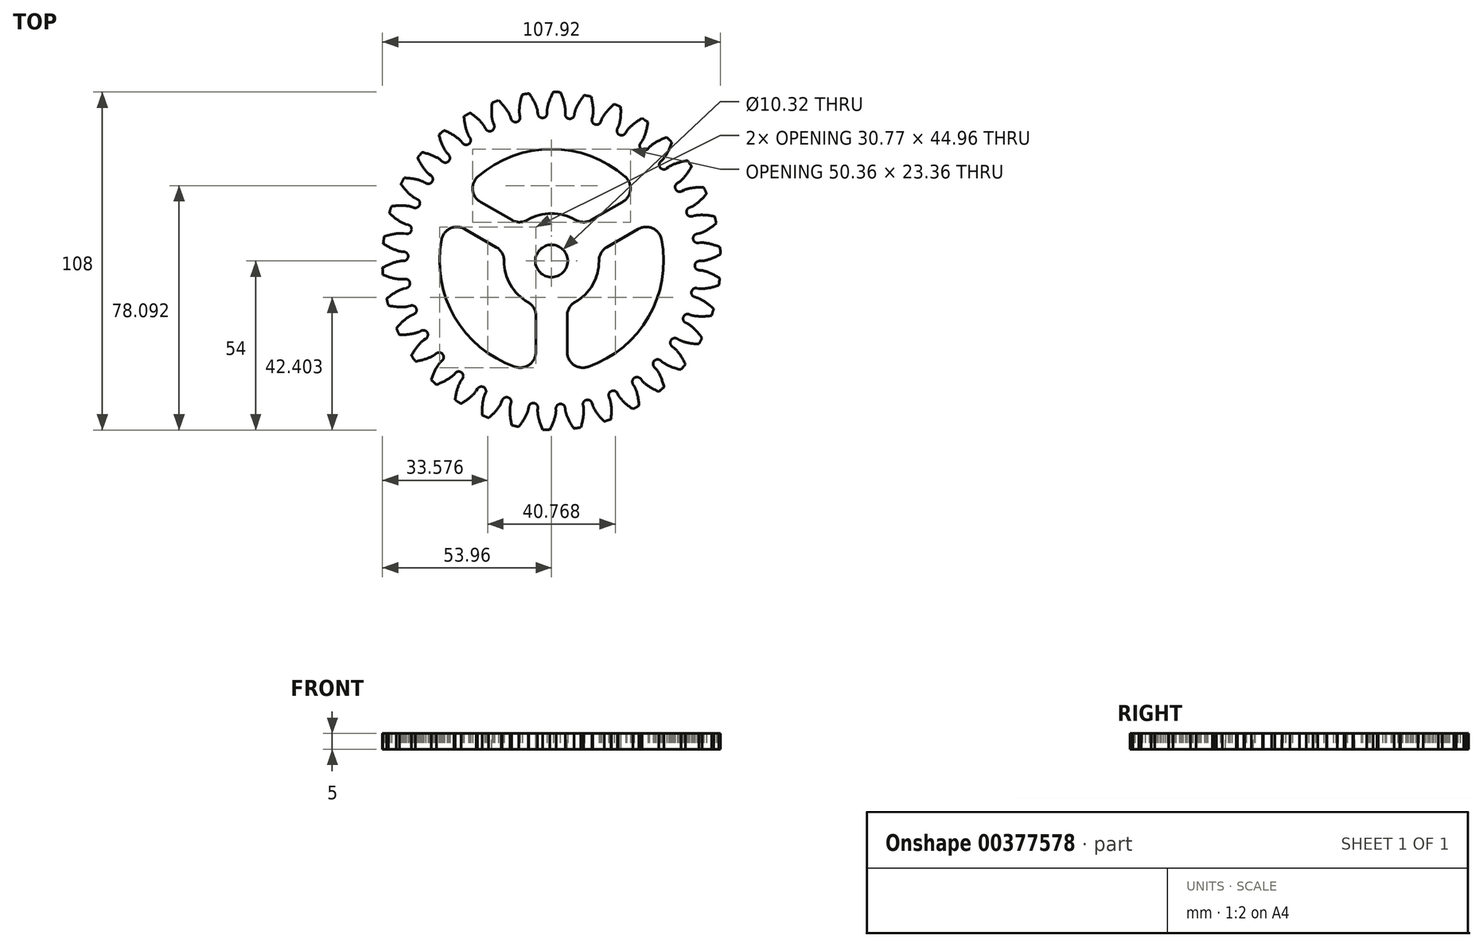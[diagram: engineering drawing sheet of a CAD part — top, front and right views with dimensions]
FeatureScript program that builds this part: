
annotation { "Feature Type Name" : "Feature", "Feature Type Description" : "" }
export const myFeature = defineFeature(function(context is Context, id is Id, definition is map)
    precondition{}
    {
        {
            assignVariable(context, id + "F0", {"name" : "T", "anyValue" : 34});
        }
        {
            assignVariable(context, id + "F1", {"name" : "SP", "anyValue" : 3});
        }
        {
            var Q0;
            Q0=qCreatedBy(makeId("Top.planeOp"),FACE);
            var sketch = newSketch(context, id + "F2", { "sketchPlane" : qUnion([Q0])});
            skCircle(sketch, "E0", {"center": v(0, 0) * mm, "radius": 54 * mm});
            skCircle(sketch, "E1", {"center": v(0, 0) * mm, "radius": 51 * mm, "construction": true});
            skCircle(sketch, "E2", {"center": v(0, 0) * mm, "radius": 47.92 * mm, "construction": true});
            skCircle(sketch, "E3", {"center": v(0, 0) * mm, "radius": 47.25 * mm});
            skLineSegment(sketch, "E4", {"start": v(0, 0) * mm, "end": v(47.92, 0) * mm});
            skFitSpline(sketch, "E5", {"points": [v(47.92, 0) * mm, v(48.06, 0) * mm, v(48.46, 0.05) * mm, v(49.12, 0.18) * mm, v(50.02, 0.42) * mm, v(51.16, 0.82) * mm, v(52.51, 1.42) * mm, v(54.05, 2.23) * mm, v(55.76, 3.3) * mm, v(57.59, 4.66) * mm, v(59.52, 6.32) * mm], "startDerivative": vector(12.01, 0.6) * mm, "endDerivative": vector(39.7, 34.22) * mm});
            skLineSegment(sketch, "E6", {"start": v(0, 0) * mm, "end": v(53.97, -1.69) * mm, "construction": true});
            skLineSegment(sketch, "E7", {"start": v(0, 0) * mm, "end": v(51, 0.76) * mm, "construction": true});
            skFitSpline(sketch, "E8.MirrorCS", {"points": [v(47.83, -3) * mm, v(47.96, -3.01) * mm, v(48.36, -3.08) * mm, v(49, -3.25) * mm, v(49.9, -3.55) * mm, v(51, -4.02) * mm, v(52.32, -4.7) * mm, v(53.8, -5.6) * mm, v(55.44, -6.79) * mm, v(57.18, -8.25) * mm, v(59, -10.03) * mm], "startDerivative": vector(11.95, -1.35) * mm, "endDerivative": vector(37.48, -36.64) * mm});
            skLineSegment(sketch, "E9", {"start": v(0, 0) * mm, "end": v(47.83, -3) * mm});
            skSolve(sketch);
        }
        {
            var Q0;
            Q0=qCreatedBy(makeId("Top.planeOp"),FACE);
            var sketch = newSketch(context, id + "F3", { "sketchPlane" : qUnion([Q0])});
            skCircle(sketch, "E10", {"center": v(0, 0) * mm, "radius": 54 * mm});
            skSolve(sketch);
        }
        {
            var Q0;
            {var subQ0=sQuery(id+"F2.wireOp",EDGE,"E5");var subQ7=sQuery(id+"F2.wireOp",EDGE,"E0");var subQ8=makeQuery(id+"F2.imprint","INTERSECT",VERTEX,{"derivedFrom":[subQ7,subQ0]});Q0=makeQuery(id+"F2.imprint","IMPRINT",FACE,{"disambiguationData":[TD([[makeQuery(id+"F2.imprint","IMPRINT",EDGE,{"disambiguationData":[TD([[subQ8,1.0]])],"derivedFrom":subQ7}),1.0]])]});}
            extrude(context, id + "F4", {"entities" : qUnion([Q0]), "depth" : 6 * mm});
        }
        {
            var Q0;
            Q0=makeQuery(id+"F4.opExtrude","CAP_FACE",FACE,{"disambiguationData":[OSD([sQuery(id+"F2.wireOp",EDGE,"E0"),sQuery(id+"F2.wireOp",EDGE,"E3"),sQuery(id+"F2.wireOp",EDGE,"E4"),sQuery(id+"F2.wireOp",EDGE,"E5"),sQuery(id+"F2.wireOp",EDGE,"E8.MirrorCS"),sQuery(id+"F2.wireOp",EDGE,"E9")])],"isStart":true});
            var sketch = newSketch(context, id + "F5", { "sketchPlane" : qUnion([Q0])});
            skCircle(sketch, "E11", {"center": v(47.23, 1.48) * mm, "radius": 1.48 * mm});
            skSolve(sketch);
        }
        {
            var Q0;
            {var subQ1=makeQuery(id+"F4.opExtrude","CAP_EDGE",EDGE,{"disambiguationData":[OSD([sQuery(id+"F2.wireOp",EDGE,"E3")])],"isStart":true});Q0=makeQuery(id+"F5.imprint","IMPRINT",FACE,{"disambiguationData":[TD([[makeQuery(id+"F5.imprint","IMPRINT",EDGE,{"derivedFrom":subQ1}),-1.0]])]});}
            extrude(context, id + "F6", {"entities" : qUnion([Q0]), "operationType" : NewBodyOperationType.ADD, "oppositeDirection" : true, "depth" : 6 * mm});
        }
        {
            var Q0;
            Q0=makeQuery(id+"F3.imprint","IMPRINT",FACE,{"disambiguationData":[TD([[makeQuery(id+"F3.imprint","IMPRINT",EDGE,{"derivedFrom":sQuery(id+"F3.wireOp",EDGE,"E10")}),1.0]])]});
            extrude(context, id + "F7", {"entities" : qUnion([Q0]), "depth" : 5 * mm});
        }
        {
            var Q0;
            Q0=makeQuery(id+"F4.opExtrude","SWEPT_BODY",BODY,{"disambiguationData":[OSD([sQuery(id+"F2.wireOp",EDGE,"E0"),sQuery(id+"F2.wireOp",EDGE,"E3"),sQuery(id+"F2.wireOp",EDGE,"E4"),sQuery(id+"F2.wireOp",EDGE,"E5"),sQuery(id+"F2.wireOp",EDGE,"E8.MirrorCS"),sQuery(id+"F2.wireOp",EDGE,"E9")])]});
            var Q1;
            Q1=makeQuery(id+"F7.opExtrude","CAP_EDGE",EDGE,{"disambiguationData":[OSD([sQuery(id+"F3.wireOp",EDGE,"E10")])],"isStart":false});
            circularPattern(context, id + "F8", {"entities" : qUnion([Q0]), "axis" : qUnion([Q1]), "angle" : 360 * degree, "instanceCount" : getVariable(context, 'T'), "equalSpace" : true});
        }
        {
            var Q0;
            Q0=makeQuery(id+"F8.opPattern","COPY",BODY,{"derivedFrom":makeQuery(id+"F4.opExtrude","SWEPT_BODY",BODY,{"disambiguationData":[OSD([sQuery(id+"F2.wireOp",EDGE,"E0"),sQuery(id+"F2.wireOp",EDGE,"E3"),sQuery(id+"F2.wireOp",EDGE,"E4"),sQuery(id+"F2.wireOp",EDGE,"E5"),sQuery(id+"F2.wireOp",EDGE,"E8.MirrorCS"),sQuery(id+"F2.wireOp",EDGE,"E9")])]}),"instanceName":"5"});
            var Q1;
            Q1=makeQuery(id+"F8.opPattern","COPY",BODY,{"derivedFrom":makeQuery(id+"F4.opExtrude","SWEPT_BODY",BODY,{"disambiguationData":[OSD([sQuery(id+"F2.wireOp",EDGE,"E0"),sQuery(id+"F2.wireOp",EDGE,"E3"),sQuery(id+"F2.wireOp",EDGE,"E4"),sQuery(id+"F2.wireOp",EDGE,"E5"),sQuery(id+"F2.wireOp",EDGE,"E8.MirrorCS"),sQuery(id+"F2.wireOp",EDGE,"E9")])]}),"instanceName":"6"});
            var Q2;
            Q2=makeQuery(id+"F8.opPattern","COPY",BODY,{"derivedFrom":makeQuery(id+"F4.opExtrude","SWEPT_BODY",BODY,{"disambiguationData":[OSD([sQuery(id+"F2.wireOp",EDGE,"E0"),sQuery(id+"F2.wireOp",EDGE,"E3"),sQuery(id+"F2.wireOp",EDGE,"E4"),sQuery(id+"F2.wireOp",EDGE,"E5"),sQuery(id+"F2.wireOp",EDGE,"E8.MirrorCS"),sQuery(id+"F2.wireOp",EDGE,"E9")])]}),"instanceName":"7"});
            var Q3;
            Q3=makeQuery(id+"F8.opPattern","COPY",BODY,{"derivedFrom":makeQuery(id+"F4.opExtrude","SWEPT_BODY",BODY,{"disambiguationData":[OSD([sQuery(id+"F2.wireOp",EDGE,"E0"),sQuery(id+"F2.wireOp",EDGE,"E3"),sQuery(id+"F2.wireOp",EDGE,"E4"),sQuery(id+"F2.wireOp",EDGE,"E5"),sQuery(id+"F2.wireOp",EDGE,"E8.MirrorCS"),sQuery(id+"F2.wireOp",EDGE,"E9")])]}),"instanceName":"8"});
            var Q4;
            Q4=makeQuery(id+"F8.opPattern","COPY",BODY,{"derivedFrom":makeQuery(id+"F4.opExtrude","SWEPT_BODY",BODY,{"disambiguationData":[OSD([sQuery(id+"F2.wireOp",EDGE,"E0"),sQuery(id+"F2.wireOp",EDGE,"E3"),sQuery(id+"F2.wireOp",EDGE,"E4"),sQuery(id+"F2.wireOp",EDGE,"E5"),sQuery(id+"F2.wireOp",EDGE,"E8.MirrorCS"),sQuery(id+"F2.wireOp",EDGE,"E9")])]}),"instanceName":"9"});
            var Q5;
            Q5=makeQuery(id+"F8.opPattern","COPY",BODY,{"derivedFrom":makeQuery(id+"F4.opExtrude","SWEPT_BODY",BODY,{"disambiguationData":[OSD([sQuery(id+"F2.wireOp",EDGE,"E0"),sQuery(id+"F2.wireOp",EDGE,"E3"),sQuery(id+"F2.wireOp",EDGE,"E4"),sQuery(id+"F2.wireOp",EDGE,"E5"),sQuery(id+"F2.wireOp",EDGE,"E8.MirrorCS"),sQuery(id+"F2.wireOp",EDGE,"E9")])]}),"instanceName":"10"});
            var Q6;
            Q6=makeQuery(id+"F8.opPattern","COPY",BODY,{"derivedFrom":makeQuery(id+"F4.opExtrude","SWEPT_BODY",BODY,{"disambiguationData":[OSD([sQuery(id+"F2.wireOp",EDGE,"E0"),sQuery(id+"F2.wireOp",EDGE,"E3"),sQuery(id+"F2.wireOp",EDGE,"E4"),sQuery(id+"F2.wireOp",EDGE,"E5"),sQuery(id+"F2.wireOp",EDGE,"E8.MirrorCS"),sQuery(id+"F2.wireOp",EDGE,"E9")])]}),"instanceName":"11"});
            var Q7;
            Q7=makeQuery(id+"F8.opPattern","COPY",BODY,{"derivedFrom":makeQuery(id+"F4.opExtrude","SWEPT_BODY",BODY,{"disambiguationData":[OSD([sQuery(id+"F2.wireOp",EDGE,"E0"),sQuery(id+"F2.wireOp",EDGE,"E3"),sQuery(id+"F2.wireOp",EDGE,"E4"),sQuery(id+"F2.wireOp",EDGE,"E5"),sQuery(id+"F2.wireOp",EDGE,"E8.MirrorCS"),sQuery(id+"F2.wireOp",EDGE,"E9")])]}),"instanceName":"12"});
            var Q8;
            Q8=makeQuery(id+"F8.opPattern","COPY",BODY,{"derivedFrom":makeQuery(id+"F4.opExtrude","SWEPT_BODY",BODY,{"disambiguationData":[OSD([sQuery(id+"F2.wireOp",EDGE,"E0"),sQuery(id+"F2.wireOp",EDGE,"E3"),sQuery(id+"F2.wireOp",EDGE,"E4"),sQuery(id+"F2.wireOp",EDGE,"E5"),sQuery(id+"F2.wireOp",EDGE,"E8.MirrorCS"),sQuery(id+"F2.wireOp",EDGE,"E9")])]}),"instanceName":"13"});
            var Q9;
            Q9=makeQuery(id+"F8.opPattern","COPY",BODY,{"derivedFrom":makeQuery(id+"F4.opExtrude","SWEPT_BODY",BODY,{"disambiguationData":[OSD([sQuery(id+"F2.wireOp",EDGE,"E0"),sQuery(id+"F2.wireOp",EDGE,"E3"),sQuery(id+"F2.wireOp",EDGE,"E4"),sQuery(id+"F2.wireOp",EDGE,"E5"),sQuery(id+"F2.wireOp",EDGE,"E8.MirrorCS"),sQuery(id+"F2.wireOp",EDGE,"E9")])]}),"instanceName":"14"});
            var Q10;
            Q10=makeQuery(id+"F8.opPattern","COPY",BODY,{"derivedFrom":makeQuery(id+"F4.opExtrude","SWEPT_BODY",BODY,{"disambiguationData":[OSD([sQuery(id+"F2.wireOp",EDGE,"E0"),sQuery(id+"F2.wireOp",EDGE,"E3"),sQuery(id+"F2.wireOp",EDGE,"E4"),sQuery(id+"F2.wireOp",EDGE,"E5"),sQuery(id+"F2.wireOp",EDGE,"E8.MirrorCS"),sQuery(id+"F2.wireOp",EDGE,"E9")])]}),"instanceName":"15"});
            var Q11;
            Q11=makeQuery(id+"F8.opPattern","COPY",BODY,{"derivedFrom":makeQuery(id+"F4.opExtrude","SWEPT_BODY",BODY,{"disambiguationData":[OSD([sQuery(id+"F2.wireOp",EDGE,"E0"),sQuery(id+"F2.wireOp",EDGE,"E3"),sQuery(id+"F2.wireOp",EDGE,"E4"),sQuery(id+"F2.wireOp",EDGE,"E5"),sQuery(id+"F2.wireOp",EDGE,"E8.MirrorCS"),sQuery(id+"F2.wireOp",EDGE,"E9")])]}),"instanceName":"16"});
            var Q12;
            Q12=makeQuery(id+"F8.opPattern","COPY",BODY,{"derivedFrom":makeQuery(id+"F4.opExtrude","SWEPT_BODY",BODY,{"disambiguationData":[OSD([sQuery(id+"F2.wireOp",EDGE,"E0"),sQuery(id+"F2.wireOp",EDGE,"E3"),sQuery(id+"F2.wireOp",EDGE,"E4"),sQuery(id+"F2.wireOp",EDGE,"E5"),sQuery(id+"F2.wireOp",EDGE,"E8.MirrorCS"),sQuery(id+"F2.wireOp",EDGE,"E9")])]}),"instanceName":"17"});
            var Q13;
            Q13=makeQuery(id+"F8.opPattern","COPY",BODY,{"derivedFrom":makeQuery(id+"F4.opExtrude","SWEPT_BODY",BODY,{"disambiguationData":[OSD([sQuery(id+"F2.wireOp",EDGE,"E0"),sQuery(id+"F2.wireOp",EDGE,"E3"),sQuery(id+"F2.wireOp",EDGE,"E4"),sQuery(id+"F2.wireOp",EDGE,"E5"),sQuery(id+"F2.wireOp",EDGE,"E8.MirrorCS"),sQuery(id+"F2.wireOp",EDGE,"E9")])]}),"instanceName":"18"});
            var Q14;
            Q14=makeQuery(id+"F8.opPattern","COPY",BODY,{"derivedFrom":makeQuery(id+"F4.opExtrude","SWEPT_BODY",BODY,{"disambiguationData":[OSD([sQuery(id+"F2.wireOp",EDGE,"E0"),sQuery(id+"F2.wireOp",EDGE,"E3"),sQuery(id+"F2.wireOp",EDGE,"E4"),sQuery(id+"F2.wireOp",EDGE,"E5"),sQuery(id+"F2.wireOp",EDGE,"E8.MirrorCS"),sQuery(id+"F2.wireOp",EDGE,"E9")])]}),"instanceName":"19"});
            var Q15;
            Q15=makeQuery(id+"F8.opPattern","COPY",BODY,{"derivedFrom":makeQuery(id+"F4.opExtrude","SWEPT_BODY",BODY,{"disambiguationData":[OSD([sQuery(id+"F2.wireOp",EDGE,"E0"),sQuery(id+"F2.wireOp",EDGE,"E3"),sQuery(id+"F2.wireOp",EDGE,"E4"),sQuery(id+"F2.wireOp",EDGE,"E5"),sQuery(id+"F2.wireOp",EDGE,"E8.MirrorCS"),sQuery(id+"F2.wireOp",EDGE,"E9")])]}),"instanceName":"20"});
            var Q16;
            Q16=makeQuery(id+"F8.opPattern","COPY",BODY,{"derivedFrom":makeQuery(id+"F4.opExtrude","SWEPT_BODY",BODY,{"disambiguationData":[OSD([sQuery(id+"F2.wireOp",EDGE,"E0"),sQuery(id+"F2.wireOp",EDGE,"E3"),sQuery(id+"F2.wireOp",EDGE,"E4"),sQuery(id+"F2.wireOp",EDGE,"E5"),sQuery(id+"F2.wireOp",EDGE,"E8.MirrorCS"),sQuery(id+"F2.wireOp",EDGE,"E9")])]}),"instanceName":"21"});
            var Q17;
            Q17=makeQuery(id+"F8.opPattern","COPY",BODY,{"derivedFrom":makeQuery(id+"F4.opExtrude","SWEPT_BODY",BODY,{"disambiguationData":[OSD([sQuery(id+"F2.wireOp",EDGE,"E0"),sQuery(id+"F2.wireOp",EDGE,"E3"),sQuery(id+"F2.wireOp",EDGE,"E4"),sQuery(id+"F2.wireOp",EDGE,"E5"),sQuery(id+"F2.wireOp",EDGE,"E8.MirrorCS"),sQuery(id+"F2.wireOp",EDGE,"E9")])]}),"instanceName":"22"});
            var Q18;
            Q18=makeQuery(id+"F8.opPattern","COPY",BODY,{"derivedFrom":makeQuery(id+"F4.opExtrude","SWEPT_BODY",BODY,{"disambiguationData":[OSD([sQuery(id+"F2.wireOp",EDGE,"E0"),sQuery(id+"F2.wireOp",EDGE,"E3"),sQuery(id+"F2.wireOp",EDGE,"E4"),sQuery(id+"F2.wireOp",EDGE,"E5"),sQuery(id+"F2.wireOp",EDGE,"E8.MirrorCS"),sQuery(id+"F2.wireOp",EDGE,"E9")])]}),"instanceName":"23"});
            var Q19;
            Q19=makeQuery(id+"F8.opPattern","COPY",BODY,{"derivedFrom":makeQuery(id+"F4.opExtrude","SWEPT_BODY",BODY,{"disambiguationData":[OSD([sQuery(id+"F2.wireOp",EDGE,"E0"),sQuery(id+"F2.wireOp",EDGE,"E3"),sQuery(id+"F2.wireOp",EDGE,"E4"),sQuery(id+"F2.wireOp",EDGE,"E5"),sQuery(id+"F2.wireOp",EDGE,"E8.MirrorCS"),sQuery(id+"F2.wireOp",EDGE,"E9")])]}),"instanceName":"24"});
            var Q20;
            Q20=makeQuery(id+"F8.opPattern","COPY",BODY,{"derivedFrom":makeQuery(id+"F4.opExtrude","SWEPT_BODY",BODY,{"disambiguationData":[OSD([sQuery(id+"F2.wireOp",EDGE,"E0"),sQuery(id+"F2.wireOp",EDGE,"E3"),sQuery(id+"F2.wireOp",EDGE,"E4"),sQuery(id+"F2.wireOp",EDGE,"E5"),sQuery(id+"F2.wireOp",EDGE,"E8.MirrorCS"),sQuery(id+"F2.wireOp",EDGE,"E9")])]}),"instanceName":"25"});
            var Q21;
            Q21=makeQuery(id+"F8.opPattern","COPY",BODY,{"derivedFrom":makeQuery(id+"F4.opExtrude","SWEPT_BODY",BODY,{"disambiguationData":[OSD([sQuery(id+"F2.wireOp",EDGE,"E0"),sQuery(id+"F2.wireOp",EDGE,"E3"),sQuery(id+"F2.wireOp",EDGE,"E4"),sQuery(id+"F2.wireOp",EDGE,"E5"),sQuery(id+"F2.wireOp",EDGE,"E8.MirrorCS"),sQuery(id+"F2.wireOp",EDGE,"E9")])]}),"instanceName":"26"});
            var Q22;
            Q22=makeQuery(id+"F8.opPattern","COPY",BODY,{"derivedFrom":makeQuery(id+"F4.opExtrude","SWEPT_BODY",BODY,{"disambiguationData":[OSD([sQuery(id+"F2.wireOp",EDGE,"E0"),sQuery(id+"F2.wireOp",EDGE,"E3"),sQuery(id+"F2.wireOp",EDGE,"E4"),sQuery(id+"F2.wireOp",EDGE,"E5"),sQuery(id+"F2.wireOp",EDGE,"E8.MirrorCS"),sQuery(id+"F2.wireOp",EDGE,"E9")])]}),"instanceName":"27"});
            var Q23;
            Q23=makeQuery(id+"F8.opPattern","COPY",BODY,{"derivedFrom":makeQuery(id+"F4.opExtrude","SWEPT_BODY",BODY,{"disambiguationData":[OSD([sQuery(id+"F2.wireOp",EDGE,"E0"),sQuery(id+"F2.wireOp",EDGE,"E3"),sQuery(id+"F2.wireOp",EDGE,"E4"),sQuery(id+"F2.wireOp",EDGE,"E5"),sQuery(id+"F2.wireOp",EDGE,"E8.MirrorCS"),sQuery(id+"F2.wireOp",EDGE,"E9")])]}),"instanceName":"28"});
            var Q24;
            Q24=makeQuery(id+"F8.opPattern","COPY",BODY,{"derivedFrom":makeQuery(id+"F4.opExtrude","SWEPT_BODY",BODY,{"disambiguationData":[OSD([sQuery(id+"F2.wireOp",EDGE,"E0"),sQuery(id+"F2.wireOp",EDGE,"E3"),sQuery(id+"F2.wireOp",EDGE,"E4"),sQuery(id+"F2.wireOp",EDGE,"E5"),sQuery(id+"F2.wireOp",EDGE,"E8.MirrorCS"),sQuery(id+"F2.wireOp",EDGE,"E9")])]}),"instanceName":"29"});
            var Q25;
            Q25=makeQuery(id+"F4.opExtrude","SWEPT_BODY",BODY,{"disambiguationData":[OSD([sQuery(id+"F2.wireOp",EDGE,"E0"),sQuery(id+"F2.wireOp",EDGE,"E3"),sQuery(id+"F2.wireOp",EDGE,"E4"),sQuery(id+"F2.wireOp",EDGE,"E5"),sQuery(id+"F2.wireOp",EDGE,"E8.MirrorCS"),sQuery(id+"F2.wireOp",EDGE,"E9")])]});
            var Q26;
            Q26=makeQuery(id+"F8.opPattern","COPY",BODY,{"derivedFrom":makeQuery(id+"F4.opExtrude","SWEPT_BODY",BODY,{"disambiguationData":[OSD([sQuery(id+"F2.wireOp",EDGE,"E0"),sQuery(id+"F2.wireOp",EDGE,"E3"),sQuery(id+"F2.wireOp",EDGE,"E4"),sQuery(id+"F2.wireOp",EDGE,"E5"),sQuery(id+"F2.wireOp",EDGE,"E8.MirrorCS"),sQuery(id+"F2.wireOp",EDGE,"E9")])]}),"instanceName":"1"});
            var Q27;
            Q27=makeQuery(id+"F8.opPattern","COPY",BODY,{"derivedFrom":makeQuery(id+"F4.opExtrude","SWEPT_BODY",BODY,{"disambiguationData":[OSD([sQuery(id+"F2.wireOp",EDGE,"E0"),sQuery(id+"F2.wireOp",EDGE,"E3"),sQuery(id+"F2.wireOp",EDGE,"E4"),sQuery(id+"F2.wireOp",EDGE,"E5"),sQuery(id+"F2.wireOp",EDGE,"E8.MirrorCS"),sQuery(id+"F2.wireOp",EDGE,"E9")])]}),"instanceName":"2"});
            var Q28;
            Q28=makeQuery(id+"F8.opPattern","COPY",BODY,{"derivedFrom":makeQuery(id+"F4.opExtrude","SWEPT_BODY",BODY,{"disambiguationData":[OSD([sQuery(id+"F2.wireOp",EDGE,"E0"),sQuery(id+"F2.wireOp",EDGE,"E3"),sQuery(id+"F2.wireOp",EDGE,"E4"),sQuery(id+"F2.wireOp",EDGE,"E5"),sQuery(id+"F2.wireOp",EDGE,"E8.MirrorCS"),sQuery(id+"F2.wireOp",EDGE,"E9")])]}),"instanceName":"3"});
            var Q29;
            Q29=makeQuery(id+"F8.opPattern","COPY",BODY,{"derivedFrom":makeQuery(id+"F4.opExtrude","SWEPT_BODY",BODY,{"disambiguationData":[OSD([sQuery(id+"F2.wireOp",EDGE,"E0"),sQuery(id+"F2.wireOp",EDGE,"E3"),sQuery(id+"F2.wireOp",EDGE,"E4"),sQuery(id+"F2.wireOp",EDGE,"E5"),sQuery(id+"F2.wireOp",EDGE,"E8.MirrorCS"),sQuery(id+"F2.wireOp",EDGE,"E9")])]}),"instanceName":"4"});
            var Q30;
            Q30=makeQuery(id+"F8.opPattern","COPY",BODY,{"derivedFrom":makeQuery(id+"F4.opExtrude","SWEPT_BODY",BODY,{"disambiguationData":[OSD([sQuery(id+"F2.wireOp",EDGE,"E0"),sQuery(id+"F2.wireOp",EDGE,"E3"),sQuery(id+"F2.wireOp",EDGE,"E5"),sQuery(id+"F2.wireOp",EDGE,"E8.MirrorCS")])]}),"instanceName":"30"});
            var Q31;
            Q31=makeQuery(id+"F8.opPattern","COPY",BODY,{"derivedFrom":makeQuery(id+"F4.opExtrude","SWEPT_BODY",BODY,{"disambiguationData":[OSD([sQuery(id+"F2.wireOp",EDGE,"E0"),sQuery(id+"F2.wireOp",EDGE,"E3"),sQuery(id+"F2.wireOp",EDGE,"E5"),sQuery(id+"F2.wireOp",EDGE,"E8.MirrorCS")])]}),"instanceName":"31"});
            var Q32;
            Q32=makeQuery(id+"F8.opPattern","COPY",BODY,{"derivedFrom":makeQuery(id+"F4.opExtrude","SWEPT_BODY",BODY,{"disambiguationData":[OSD([sQuery(id+"F2.wireOp",EDGE,"E0"),sQuery(id+"F2.wireOp",EDGE,"E3"),sQuery(id+"F2.wireOp",EDGE,"E5"),sQuery(id+"F2.wireOp",EDGE,"E8.MirrorCS")])]}),"instanceName":"32"});
            var Q33;
            Q33=makeQuery(id+"F8.opPattern","COPY",BODY,{"derivedFrom":makeQuery(id+"F4.opExtrude","SWEPT_BODY",BODY,{"disambiguationData":[OSD([sQuery(id+"F2.wireOp",EDGE,"E0"),sQuery(id+"F2.wireOp",EDGE,"E3"),sQuery(id+"F2.wireOp",EDGE,"E5"),sQuery(id+"F2.wireOp",EDGE,"E8.MirrorCS")])]}),"instanceName":"33"});
            var Q34;
            Q34=makeQuery(id+"F8.opPattern","COPY",BODY,{"derivedFrom":makeQuery(id+"F4.opExtrude","SWEPT_BODY",BODY,{"disambiguationData":[OSD([sQuery(id+"F2.wireOp",EDGE,"E0"),sQuery(id+"F2.wireOp",EDGE,"E3"),sQuery(id+"F2.wireOp",EDGE,"E5"),sQuery(id+"F2.wireOp",EDGE,"E8.MirrorCS")])]}),"instanceName":"34"});
            var Q35;
            Q35=makeQuery(id+"F8.opPattern","COPY",BODY,{"derivedFrom":makeQuery(id+"F4.opExtrude","SWEPT_BODY",BODY,{"disambiguationData":[OSD([sQuery(id+"F2.wireOp",EDGE,"E0"),sQuery(id+"F2.wireOp",EDGE,"E3"),sQuery(id+"F2.wireOp",EDGE,"E5"),sQuery(id+"F2.wireOp",EDGE,"E8.MirrorCS")])]}),"instanceName":"35"});
            var Q36;
            Q36=makeQuery(id+"F8.opPattern","COPY",BODY,{"derivedFrom":makeQuery(id+"F4.opExtrude","SWEPT_BODY",BODY,{"disambiguationData":[OSD([sQuery(id+"F2.wireOp",EDGE,"E0"),sQuery(id+"F2.wireOp",EDGE,"E3"),sQuery(id+"F2.wireOp",EDGE,"E5"),sQuery(id+"F2.wireOp",EDGE,"E8.MirrorCS")])]}),"instanceName":"36"});
            var Q37;
            Q37=makeQuery(id+"F8.opPattern","COPY",BODY,{"derivedFrom":makeQuery(id+"F4.opExtrude","SWEPT_BODY",BODY,{"disambiguationData":[OSD([sQuery(id+"F2.wireOp",EDGE,"E0"),sQuery(id+"F2.wireOp",EDGE,"E3"),sQuery(id+"F2.wireOp",EDGE,"E5"),sQuery(id+"F2.wireOp",EDGE,"E8.MirrorCS")])]}),"instanceName":"37"});
            var Q38;
            Q38=makeQuery(id+"F8.opPattern","COPY",BODY,{"derivedFrom":makeQuery(id+"F4.opExtrude","SWEPT_BODY",BODY,{"disambiguationData":[OSD([sQuery(id+"F2.wireOp",EDGE,"E0"),sQuery(id+"F2.wireOp",EDGE,"E3"),sQuery(id+"F2.wireOp",EDGE,"E5"),sQuery(id+"F2.wireOp",EDGE,"E8.MirrorCS")])]}),"instanceName":"38"});
            var Q39;
            Q39=makeQuery(id+"F8.opPattern","COPY",BODY,{"derivedFrom":makeQuery(id+"F4.opExtrude","SWEPT_BODY",BODY,{"disambiguationData":[OSD([sQuery(id+"F2.wireOp",EDGE,"E0"),sQuery(id+"F2.wireOp",EDGE,"E3"),sQuery(id+"F2.wireOp",EDGE,"E5"),sQuery(id+"F2.wireOp",EDGE,"E8.MirrorCS")])]}),"instanceName":"39"});
            var Q40;
            Q40=makeQuery(id+"F8.opPattern","COPY",BODY,{"derivedFrom":makeQuery(id+"F4.opExtrude","SWEPT_BODY",BODY,{"disambiguationData":[OSD([sQuery(id+"F2.wireOp",EDGE,"E0"),sQuery(id+"F2.wireOp",EDGE,"E3"),sQuery(id+"F2.wireOp",EDGE,"E5"),sQuery(id+"F2.wireOp",EDGE,"E8.MirrorCS")])]}),"instanceName":"40"});
            var Q41;
            Q41=makeQuery(id+"F8.opPattern","COPY",BODY,{"derivedFrom":makeQuery(id+"F4.opExtrude","SWEPT_BODY",BODY,{"disambiguationData":[OSD([sQuery(id+"F2.wireOp",EDGE,"E0"),sQuery(id+"F2.wireOp",EDGE,"E3"),sQuery(id+"F2.wireOp",EDGE,"E5"),sQuery(id+"F2.wireOp",EDGE,"E8.MirrorCS")])]}),"instanceName":"41"});
            var Q42;
            Q42=makeQuery(id+"F8.opPattern","COPY",BODY,{"derivedFrom":makeQuery(id+"F4.opExtrude","SWEPT_BODY",BODY,{"disambiguationData":[OSD([sQuery(id+"F2.wireOp",EDGE,"E0"),sQuery(id+"F2.wireOp",EDGE,"E3"),sQuery(id+"F2.wireOp",EDGE,"E5"),sQuery(id+"F2.wireOp",EDGE,"E8.MirrorCS")])]}),"instanceName":"42"});
            var Q43;
            Q43=makeQuery(id+"F8.opPattern","COPY",BODY,{"derivedFrom":makeQuery(id+"F4.opExtrude","SWEPT_BODY",BODY,{"disambiguationData":[OSD([sQuery(id+"F2.wireOp",EDGE,"E0"),sQuery(id+"F2.wireOp",EDGE,"E3"),sQuery(id+"F2.wireOp",EDGE,"E5"),sQuery(id+"F2.wireOp",EDGE,"E8.MirrorCS")])]}),"instanceName":"43"});
            var Q44;
            Q44=makeQuery(id+"F8.opPattern","COPY",BODY,{"derivedFrom":makeQuery(id+"F4.opExtrude","SWEPT_BODY",BODY,{"disambiguationData":[OSD([sQuery(id+"F2.wireOp",EDGE,"E0"),sQuery(id+"F2.wireOp",EDGE,"E3"),sQuery(id+"F2.wireOp",EDGE,"E5"),sQuery(id+"F2.wireOp",EDGE,"E8.MirrorCS")])]}),"instanceName":"44"});
            var Q45;
            Q45=makeQuery(id+"F8.opPattern","COPY",BODY,{"derivedFrom":makeQuery(id+"F4.opExtrude","SWEPT_BODY",BODY,{"disambiguationData":[OSD([sQuery(id+"F2.wireOp",EDGE,"E0"),sQuery(id+"F2.wireOp",EDGE,"E3"),sQuery(id+"F2.wireOp",EDGE,"E5"),sQuery(id+"F2.wireOp",EDGE,"E8.MirrorCS")])]}),"instanceName":"45"});
            var Q46;
            Q46=makeQuery(id+"F8.opPattern","COPY",BODY,{"derivedFrom":makeQuery(id+"F4.opExtrude","SWEPT_BODY",BODY,{"disambiguationData":[OSD([sQuery(id+"F2.wireOp",EDGE,"E0"),sQuery(id+"F2.wireOp",EDGE,"E3"),sQuery(id+"F2.wireOp",EDGE,"E5"),sQuery(id+"F2.wireOp",EDGE,"E8.MirrorCS")])]}),"instanceName":"46"});
            var Q47;
            Q47=makeQuery(id+"F8.opPattern","COPY",BODY,{"derivedFrom":makeQuery(id+"F4.opExtrude","SWEPT_BODY",BODY,{"disambiguationData":[OSD([sQuery(id+"F2.wireOp",EDGE,"E0"),sQuery(id+"F2.wireOp",EDGE,"E3"),sQuery(id+"F2.wireOp",EDGE,"E5"),sQuery(id+"F2.wireOp",EDGE,"E8.MirrorCS")])]}),"instanceName":"47"});
            var Q48;
            Q48=makeQuery(id+"F8.opPattern","COPY",BODY,{"derivedFrom":makeQuery(id+"F4.opExtrude","SWEPT_BODY",BODY,{"disambiguationData":[OSD([sQuery(id+"F2.wireOp",EDGE,"E0"),sQuery(id+"F2.wireOp",EDGE,"E3"),sQuery(id+"F2.wireOp",EDGE,"E5"),sQuery(id+"F2.wireOp",EDGE,"E8.MirrorCS")])]}),"instanceName":"48"});
            var Q49;
            Q49=makeQuery(id+"F8.opPattern","COPY",BODY,{"derivedFrom":makeQuery(id+"F4.opExtrude","SWEPT_BODY",BODY,{"disambiguationData":[OSD([sQuery(id+"F2.wireOp",EDGE,"E0"),sQuery(id+"F2.wireOp",EDGE,"E3"),sQuery(id+"F2.wireOp",EDGE,"E5"),sQuery(id+"F2.wireOp",EDGE,"E8.MirrorCS")])]}),"instanceName":"49"});
            var Q50;
            Q50=makeQuery(id+"F8.opPattern","COPY",BODY,{"derivedFrom":makeQuery(id+"F4.opExtrude","SWEPT_BODY",BODY,{"disambiguationData":[OSD([sQuery(id+"F2.wireOp",EDGE,"E0"),sQuery(id+"F2.wireOp",EDGE,"E3"),sQuery(id+"F2.wireOp",EDGE,"E5"),sQuery(id+"F2.wireOp",EDGE,"E8.MirrorCS")])]}),"instanceName":"50"});
            var Q51;
            Q51=makeQuery(id+"F8.opPattern","COPY",BODY,{"derivedFrom":makeQuery(id+"F4.opExtrude","SWEPT_BODY",BODY,{"disambiguationData":[OSD([sQuery(id+"F2.wireOp",EDGE,"E0"),sQuery(id+"F2.wireOp",EDGE,"E3"),sQuery(id+"F2.wireOp",EDGE,"E5"),sQuery(id+"F2.wireOp",EDGE,"E8.MirrorCS")])]}),"instanceName":"51"});
            var Q52;
            Q52=makeQuery(id+"F8.opPattern","COPY",BODY,{"derivedFrom":makeQuery(id+"F4.opExtrude","SWEPT_BODY",BODY,{"disambiguationData":[OSD([sQuery(id+"F2.wireOp",EDGE,"E0"),sQuery(id+"F2.wireOp",EDGE,"E3"),sQuery(id+"F2.wireOp",EDGE,"E5"),sQuery(id+"F2.wireOp",EDGE,"E8.MirrorCS")])]}),"instanceName":"52"});
            var Q53;
            Q53=makeQuery(id+"F8.opPattern","COPY",BODY,{"derivedFrom":makeQuery(id+"F4.opExtrude","SWEPT_BODY",BODY,{"disambiguationData":[OSD([sQuery(id+"F2.wireOp",EDGE,"E0"),sQuery(id+"F2.wireOp",EDGE,"E3"),sQuery(id+"F2.wireOp",EDGE,"E5"),sQuery(id+"F2.wireOp",EDGE,"E8.MirrorCS")])]}),"instanceName":"53"});
            var Q54;
            Q54=makeQuery(id+"F8.opPattern","COPY",BODY,{"derivedFrom":makeQuery(id+"F4.opExtrude","SWEPT_BODY",BODY,{"disambiguationData":[OSD([sQuery(id+"F2.wireOp",EDGE,"E0"),sQuery(id+"F2.wireOp",EDGE,"E3"),sQuery(id+"F2.wireOp",EDGE,"E5"),sQuery(id+"F2.wireOp",EDGE,"E8.MirrorCS")])]}),"instanceName":"54"});
            var Q55;
            Q55=makeQuery(id+"F8.opPattern","COPY",BODY,{"derivedFrom":makeQuery(id+"F4.opExtrude","SWEPT_BODY",BODY,{"disambiguationData":[OSD([sQuery(id+"F2.wireOp",EDGE,"E0"),sQuery(id+"F2.wireOp",EDGE,"E3"),sQuery(id+"F2.wireOp",EDGE,"E5"),sQuery(id+"F2.wireOp",EDGE,"E8.MirrorCS")])]}),"instanceName":"55"});
            var Q56;
            Q56=makeQuery(id+"F8.opPattern","COPY",BODY,{"derivedFrom":makeQuery(id+"F4.opExtrude","SWEPT_BODY",BODY,{"disambiguationData":[OSD([sQuery(id+"F2.wireOp",EDGE,"E0"),sQuery(id+"F2.wireOp",EDGE,"E3"),sQuery(id+"F2.wireOp",EDGE,"E5"),sQuery(id+"F2.wireOp",EDGE,"E8.MirrorCS")])]}),"instanceName":"56"});
            var Q57;
            Q57=makeQuery(id+"F8.opPattern","COPY",BODY,{"derivedFrom":makeQuery(id+"F4.opExtrude","SWEPT_BODY",BODY,{"disambiguationData":[OSD([sQuery(id+"F2.wireOp",EDGE,"E0"),sQuery(id+"F2.wireOp",EDGE,"E3"),sQuery(id+"F2.wireOp",EDGE,"E5"),sQuery(id+"F2.wireOp",EDGE,"E8.MirrorCS")])]}),"instanceName":"57"});
            var Q58;
            Q58=makeQuery(id+"F8.opPattern","COPY",BODY,{"derivedFrom":makeQuery(id+"F4.opExtrude","SWEPT_BODY",BODY,{"disambiguationData":[OSD([sQuery(id+"F2.wireOp",EDGE,"E0"),sQuery(id+"F2.wireOp",EDGE,"E3"),sQuery(id+"F2.wireOp",EDGE,"E5"),sQuery(id+"F2.wireOp",EDGE,"E8.MirrorCS")])]}),"instanceName":"58"});
            var Q59;
            Q59=makeQuery(id+"F8.opPattern","COPY",BODY,{"derivedFrom":makeQuery(id+"F4.opExtrude","SWEPT_BODY",BODY,{"disambiguationData":[OSD([sQuery(id+"F2.wireOp",EDGE,"E0"),sQuery(id+"F2.wireOp",EDGE,"E3"),sQuery(id+"F2.wireOp",EDGE,"E5"),sQuery(id+"F2.wireOp",EDGE,"E8.MirrorCS")])]}),"instanceName":"59"});
            var Q60;
            Q60=makeQuery(id+"F8.opPattern","COPY",BODY,{"derivedFrom":makeQuery(id+"F4.opExtrude","SWEPT_BODY",BODY,{"disambiguationData":[OSD([sQuery(id+"F2.wireOp",EDGE,"E0"),sQuery(id+"F2.wireOp",EDGE,"E3"),sQuery(id+"F2.wireOp",EDGE,"E5"),sQuery(id+"F2.wireOp",EDGE,"E8.MirrorCS")])]}),"instanceName":"60"});
            var Q61;
            Q61=makeQuery(id+"F8.opPattern","COPY",BODY,{"derivedFrom":makeQuery(id+"F4.opExtrude","SWEPT_BODY",BODY,{"disambiguationData":[OSD([sQuery(id+"F2.wireOp",EDGE,"E0"),sQuery(id+"F2.wireOp",EDGE,"E3"),sQuery(id+"F2.wireOp",EDGE,"E5"),sQuery(id+"F2.wireOp",EDGE,"E8.MirrorCS")])]}),"instanceName":"61"});
            var Q62;
            Q62=makeQuery(id+"F8.opPattern","COPY",BODY,{"derivedFrom":makeQuery(id+"F4.opExtrude","SWEPT_BODY",BODY,{"disambiguationData":[OSD([sQuery(id+"F2.wireOp",EDGE,"E0"),sQuery(id+"F2.wireOp",EDGE,"E3"),sQuery(id+"F2.wireOp",EDGE,"E5"),sQuery(id+"F2.wireOp",EDGE,"E8.MirrorCS")])]}),"instanceName":"62"});
            var Q63;
            Q63=makeQuery(id+"F8.opPattern","COPY",BODY,{"derivedFrom":makeQuery(id+"F4.opExtrude","SWEPT_BODY",BODY,{"disambiguationData":[OSD([sQuery(id+"F2.wireOp",EDGE,"E0"),sQuery(id+"F2.wireOp",EDGE,"E3"),sQuery(id+"F2.wireOp",EDGE,"E5"),sQuery(id+"F2.wireOp",EDGE,"E8.MirrorCS")])]}),"instanceName":"63"});
            var Q64;
            Q64=makeQuery(id+"F8.opPattern","COPY",BODY,{"derivedFrom":makeQuery(id+"F4.opExtrude","SWEPT_BODY",BODY,{"disambiguationData":[OSD([sQuery(id+"F2.wireOp",EDGE,"E0"),sQuery(id+"F2.wireOp",EDGE,"E3"),sQuery(id+"F2.wireOp",EDGE,"E5"),sQuery(id+"F2.wireOp",EDGE,"E8.MirrorCS")])]}),"instanceName":"64"});
            var Q65;
            Q65=makeQuery(id+"F8.opPattern","COPY",BODY,{"derivedFrom":makeQuery(id+"F4.opExtrude","SWEPT_BODY",BODY,{"disambiguationData":[OSD([sQuery(id+"F2.wireOp",EDGE,"E0"),sQuery(id+"F2.wireOp",EDGE,"E3"),sQuery(id+"F2.wireOp",EDGE,"E5"),sQuery(id+"F2.wireOp",EDGE,"E8.MirrorCS")])]}),"instanceName":"65"});
            var Q66;
            Q66=makeQuery(id+"F8.opPattern","COPY",BODY,{"derivedFrom":makeQuery(id+"F4.opExtrude","SWEPT_BODY",BODY,{"disambiguationData":[OSD([sQuery(id+"F2.wireOp",EDGE,"E0"),sQuery(id+"F2.wireOp",EDGE,"E3"),sQuery(id+"F2.wireOp",EDGE,"E5"),sQuery(id+"F2.wireOp",EDGE,"E8.MirrorCS")])]}),"instanceName":"66"});
            var Q67;
            Q67=makeQuery(id+"F8.opPattern","COPY",BODY,{"derivedFrom":makeQuery(id+"F4.opExtrude","SWEPT_BODY",BODY,{"disambiguationData":[OSD([sQuery(id+"F2.wireOp",EDGE,"E0"),sQuery(id+"F2.wireOp",EDGE,"E3"),sQuery(id+"F2.wireOp",EDGE,"E5"),sQuery(id+"F2.wireOp",EDGE,"E8.MirrorCS")])]}),"instanceName":"67"});
            var Q68;
            Q68=makeQuery(id+"F8.opPattern","COPY",BODY,{"derivedFrom":makeQuery(id+"F4.opExtrude","SWEPT_BODY",BODY,{"disambiguationData":[OSD([sQuery(id+"F2.wireOp",EDGE,"E0"),sQuery(id+"F2.wireOp",EDGE,"E3"),sQuery(id+"F2.wireOp",EDGE,"E5"),sQuery(id+"F2.wireOp",EDGE,"E8.MirrorCS")])]}),"instanceName":"68"});
            var Q69;
            Q69=makeQuery(id+"F8.opPattern","COPY",BODY,{"derivedFrom":makeQuery(id+"F4.opExtrude","SWEPT_BODY",BODY,{"disambiguationData":[OSD([sQuery(id+"F2.wireOp",EDGE,"E0"),sQuery(id+"F2.wireOp",EDGE,"E3"),sQuery(id+"F2.wireOp",EDGE,"E5"),sQuery(id+"F2.wireOp",EDGE,"E8.MirrorCS")])]}),"instanceName":"69"});
            var Q70;
            Q70=makeQuery(id+"F8.opPattern","COPY",BODY,{"derivedFrom":makeQuery(id+"F4.opExtrude","SWEPT_BODY",BODY,{"disambiguationData":[OSD([sQuery(id+"F2.wireOp",EDGE,"E0"),sQuery(id+"F2.wireOp",EDGE,"E3"),sQuery(id+"F2.wireOp",EDGE,"E5"),sQuery(id+"F2.wireOp",EDGE,"E8.MirrorCS")])]}),"instanceName":"70"});
            var Q71;
            Q71=makeQuery(id+"F8.opPattern","COPY",BODY,{"derivedFrom":makeQuery(id+"F4.opExtrude","SWEPT_BODY",BODY,{"disambiguationData":[OSD([sQuery(id+"F2.wireOp",EDGE,"E0"),sQuery(id+"F2.wireOp",EDGE,"E3"),sQuery(id+"F2.wireOp",EDGE,"E5"),sQuery(id+"F2.wireOp",EDGE,"E8.MirrorCS")])]}),"instanceName":"71"});
            var Q72;
            Q72=makeQuery(id+"F8.opPattern","COPY",BODY,{"derivedFrom":makeQuery(id+"F4.opExtrude","SWEPT_BODY",BODY,{"disambiguationData":[OSD([sQuery(id+"F2.wireOp",EDGE,"E0"),sQuery(id+"F2.wireOp",EDGE,"E3"),sQuery(id+"F2.wireOp",EDGE,"E5"),sQuery(id+"F2.wireOp",EDGE,"E8.MirrorCS")])]}),"instanceName":"72"});
            var Q73;
            Q73=makeQuery(id+"F8.opPattern","COPY",BODY,{"derivedFrom":makeQuery(id+"F4.opExtrude","SWEPT_BODY",BODY,{"disambiguationData":[OSD([sQuery(id+"F2.wireOp",EDGE,"E0"),sQuery(id+"F2.wireOp",EDGE,"E3"),sQuery(id+"F2.wireOp",EDGE,"E5"),sQuery(id+"F2.wireOp",EDGE,"E8.MirrorCS")])]}),"instanceName":"73"});
            var Q74;
            Q74=makeQuery(id+"F8.opPattern","COPY",BODY,{"derivedFrom":makeQuery(id+"F4.opExtrude","SWEPT_BODY",BODY,{"disambiguationData":[OSD([sQuery(id+"F2.wireOp",EDGE,"E0"),sQuery(id+"F2.wireOp",EDGE,"E3"),sQuery(id+"F2.wireOp",EDGE,"E5"),sQuery(id+"F2.wireOp",EDGE,"E8.MirrorCS")])]}),"instanceName":"74"});
            var Q75;
            Q75=makeQuery(id+"F8.opPattern","COPY",BODY,{"derivedFrom":makeQuery(id+"F4.opExtrude","SWEPT_BODY",BODY,{"disambiguationData":[OSD([sQuery(id+"F2.wireOp",EDGE,"E0"),sQuery(id+"F2.wireOp",EDGE,"E3"),sQuery(id+"F2.wireOp",EDGE,"E5"),sQuery(id+"F2.wireOp",EDGE,"E8.MirrorCS")])]}),"instanceName":"75"});
            var Q76;
            Q76=makeQuery(id+"F8.opPattern","COPY",BODY,{"derivedFrom":makeQuery(id+"F4.opExtrude","SWEPT_BODY",BODY,{"disambiguationData":[OSD([sQuery(id+"F2.wireOp",EDGE,"E0"),sQuery(id+"F2.wireOp",EDGE,"E3"),sQuery(id+"F2.wireOp",EDGE,"E5"),sQuery(id+"F2.wireOp",EDGE,"E8.MirrorCS")])]}),"instanceName":"76"});
            var Q77;
            Q77=makeQuery(id+"F8.opPattern","COPY",BODY,{"derivedFrom":makeQuery(id+"F4.opExtrude","SWEPT_BODY",BODY,{"disambiguationData":[OSD([sQuery(id+"F2.wireOp",EDGE,"E0"),sQuery(id+"F2.wireOp",EDGE,"E3"),sQuery(id+"F2.wireOp",EDGE,"E5"),sQuery(id+"F2.wireOp",EDGE,"E8.MirrorCS")])]}),"instanceName":"77"});
            var Q78;
            Q78=makeQuery(id+"F8.opPattern","COPY",BODY,{"derivedFrom":makeQuery(id+"F4.opExtrude","SWEPT_BODY",BODY,{"disambiguationData":[OSD([sQuery(id+"F2.wireOp",EDGE,"E0"),sQuery(id+"F2.wireOp",EDGE,"E3"),sQuery(id+"F2.wireOp",EDGE,"E5"),sQuery(id+"F2.wireOp",EDGE,"E8.MirrorCS")])]}),"instanceName":"78"});
            var Q79;
            Q79=makeQuery(id+"F8.opPattern","COPY",BODY,{"derivedFrom":makeQuery(id+"F4.opExtrude","SWEPT_BODY",BODY,{"disambiguationData":[OSD([sQuery(id+"F2.wireOp",EDGE,"E0"),sQuery(id+"F2.wireOp",EDGE,"E3"),sQuery(id+"F2.wireOp",EDGE,"E5"),sQuery(id+"F2.wireOp",EDGE,"E8.MirrorCS")])]}),"instanceName":"79"});
            var Q80;
            Q80=makeQuery(id+"F8.opPattern","COPY",BODY,{"derivedFrom":makeQuery(id+"F4.opExtrude","SWEPT_BODY",BODY,{"disambiguationData":[OSD([sQuery(id+"F2.wireOp",EDGE,"E0"),sQuery(id+"F2.wireOp",EDGE,"E3"),sQuery(id+"F2.wireOp",EDGE,"E5"),sQuery(id+"F2.wireOp",EDGE,"E8.MirrorCS")])]}),"instanceName":"80"});
            var Q81;
            Q81=makeQuery(id+"F8.opPattern","COPY",BODY,{"derivedFrom":makeQuery(id+"F4.opExtrude","SWEPT_BODY",BODY,{"disambiguationData":[OSD([sQuery(id+"F2.wireOp",EDGE,"E0"),sQuery(id+"F2.wireOp",EDGE,"E3"),sQuery(id+"F2.wireOp",EDGE,"E5"),sQuery(id+"F2.wireOp",EDGE,"E8.MirrorCS")])]}),"instanceName":"81"});
            var Q82;
            Q82=makeQuery(id+"F8.opPattern","COPY",BODY,{"derivedFrom":makeQuery(id+"F4.opExtrude","SWEPT_BODY",BODY,{"disambiguationData":[OSD([sQuery(id+"F2.wireOp",EDGE,"E0"),sQuery(id+"F2.wireOp",EDGE,"E3"),sQuery(id+"F2.wireOp",EDGE,"E5"),sQuery(id+"F2.wireOp",EDGE,"E8.MirrorCS")])]}),"instanceName":"82"});
            var Q83;
            Q83=makeQuery(id+"F8.opPattern","COPY",BODY,{"derivedFrom":makeQuery(id+"F4.opExtrude","SWEPT_BODY",BODY,{"disambiguationData":[OSD([sQuery(id+"F2.wireOp",EDGE,"E0"),sQuery(id+"F2.wireOp",EDGE,"E3"),sQuery(id+"F2.wireOp",EDGE,"E5"),sQuery(id+"F2.wireOp",EDGE,"E8.MirrorCS")])]}),"instanceName":"83"});
            var Q84;
            Q84=makeQuery(id+"F8.opPattern","COPY",BODY,{"derivedFrom":makeQuery(id+"F4.opExtrude","SWEPT_BODY",BODY,{"disambiguationData":[OSD([sQuery(id+"F2.wireOp",EDGE,"E0"),sQuery(id+"F2.wireOp",EDGE,"E3"),sQuery(id+"F2.wireOp",EDGE,"E5"),sQuery(id+"F2.wireOp",EDGE,"E8.MirrorCS")])]}),"instanceName":"84"});
            var Q85;
            Q85=makeQuery(id+"F8.opPattern","COPY",BODY,{"derivedFrom":makeQuery(id+"F4.opExtrude","SWEPT_BODY",BODY,{"disambiguationData":[OSD([sQuery(id+"F2.wireOp",EDGE,"E0"),sQuery(id+"F2.wireOp",EDGE,"E3"),sQuery(id+"F2.wireOp",EDGE,"E5"),sQuery(id+"F2.wireOp",EDGE,"E8.MirrorCS")])]}),"instanceName":"85"});
            var Q86;
            Q86=makeQuery(id+"F8.opPattern","COPY",BODY,{"derivedFrom":makeQuery(id+"F4.opExtrude","SWEPT_BODY",BODY,{"disambiguationData":[OSD([sQuery(id+"F2.wireOp",EDGE,"E0"),sQuery(id+"F2.wireOp",EDGE,"E3"),sQuery(id+"F2.wireOp",EDGE,"E5"),sQuery(id+"F2.wireOp",EDGE,"E8.MirrorCS")])]}),"instanceName":"86"});
            var Q87;
            Q87=makeQuery(id+"F8.opPattern","COPY",BODY,{"derivedFrom":makeQuery(id+"F4.opExtrude","SWEPT_BODY",BODY,{"disambiguationData":[OSD([sQuery(id+"F2.wireOp",EDGE,"E0"),sQuery(id+"F2.wireOp",EDGE,"E3"),sQuery(id+"F2.wireOp",EDGE,"E5"),sQuery(id+"F2.wireOp",EDGE,"E8.MirrorCS")])]}),"instanceName":"87"});
            var Q88;
            Q88=makeQuery(id+"F8.opPattern","COPY",BODY,{"derivedFrom":makeQuery(id+"F4.opExtrude","SWEPT_BODY",BODY,{"disambiguationData":[OSD([sQuery(id+"F2.wireOp",EDGE,"E0"),sQuery(id+"F2.wireOp",EDGE,"E3"),sQuery(id+"F2.wireOp",EDGE,"E5"),sQuery(id+"F2.wireOp",EDGE,"E8.MirrorCS")])]}),"instanceName":"88"});
            var Q89;
            Q89=makeQuery(id+"F8.opPattern","COPY",BODY,{"derivedFrom":makeQuery(id+"F4.opExtrude","SWEPT_BODY",BODY,{"disambiguationData":[OSD([sQuery(id+"F2.wireOp",EDGE,"E0"),sQuery(id+"F2.wireOp",EDGE,"E3"),sQuery(id+"F2.wireOp",EDGE,"E5"),sQuery(id+"F2.wireOp",EDGE,"E8.MirrorCS")])]}),"instanceName":"89"});
            var Q90;
            Q90=makeQuery(id+"F7.opExtrude","SWEPT_BODY",BODY,{"disambiguationData":[OSD([sQuery(id+"F3.wireOp",EDGE,"E10")])]});
            booleanBodies(context, id + "F9", {"operationType" : BooleanOperationType.SUBTRACTION, "tools" : qUnion([Q0, Q1, Q2, Q3, Q4, Q5, Q6, Q7, Q8, Q9, Q10, Q11, Q12, Q13, Q14, Q15, Q16, Q17, Q18, Q19, Q20, Q21, Q22, Q23, Q24, Q25, Q26, Q27, Q28, Q29, Q30, Q31, Q32, Q33, Q34, Q35, Q36, Q37, Q38, Q39, Q40, Q41, Q42, Q43, Q44, Q45, Q46, Q47, Q48, Q49, Q50, Q51, Q52, Q53, Q54, Q55, Q56, Q57, Q58, Q59, Q60, Q61, Q62, Q63, Q64, Q65, Q66, Q67, Q68, Q69, Q70, Q71, Q72, Q73, Q74, Q75, Q76, Q77, Q78, Q79, Q80, Q81, Q82, Q83, Q84, Q85, Q86, Q87, Q88, Q89]), "targets" : qUnion([Q90])});
        }
        {
            var Q0;
            Q0=makeQuery(id+"F7.opExtrude","CAP_FACE",FACE,{"disambiguationData":[OSD([sQuery(id+"F3.wireOp",EDGE,"E10")])],"isStart":true});
            var sketch = newSketch(context, id + "F10", { "sketchPlane" : qUnion([Q0])});
            skCircle(sketch, "E12", {"center": v(0, 0) * mm, "radius": 5.16 * mm});
            skCircle(sketch, "E13", {"center": v(0, 0) * mm, "radius": 15.16 * mm});
            skCircle(sketch, "E14", {"center": v(0, 0) * mm, "radius": 35.77 * mm});
            skLineSegment(sketch, "E15", {"start": v(0, 0) * mm, "end": v(0, 35.77) * mm, "construction": true});
            skLineSegment(sketch, "E16.0", {"start": v(5, 0) * mm, "end": v(5, 35.42) * mm});
            skLineSegment(sketch, "E17", {"start": v(0, 0) * mm, "end": v(39.64, -22.89) * mm, "construction": true});
            skLineSegment(sketch, "E18.0", {"start": v(2.5, 4.33) * mm, "end": v(41.9, -18.42) * mm});
            skCircle(sketch, "E19", {"center": v(0, 0) * mm, "radius": 45.77 * mm});
            skSolve(sketch);
        }
        {
            var Q0;
            Q0=makeQuery(id+"F10.imprint","IMPRINT",FACE,{"disambiguationData":[TD([[makeQuery(id+"F10.imprint","IMPRINT",EDGE,{"derivedFrom":sQuery(id+"F10.wireOp",EDGE,"E12")}),1.0]])]});
            extrude(context, id + "F11", {"entities" : qUnion([Q0]), "operationType" : NewBodyOperationType.REMOVE, "oppositeDirection" : true, "depth" : 25 * mm});
        }
        {
            var Q0;
            {var subQ0=sQuery(id+"F10.wireOp",EDGE,"E16.0");var subQ1=sQuery(id+"F10.wireOp",EDGE,"E13");var subQ2=makeQuery(id+"F10.imprint","INTERSECT",VERTEX,{"derivedFrom":[subQ1,subQ0]});Q0=makeQuery(id+"F10.imprint","IMPRINT",FACE,{"disambiguationData":[TD([[makeQuery(id+"F10.imprint","IMPRINT",EDGE,{"disambiguationData":[TD([[subQ2,1.0]])],"derivedFrom":subQ1}),-1.0]])]});}
            extrude(context, id + "F12", {"entities" : qUnion([Q0]), "oppositeDirection" : true, "depth" : 6 * mm});
        }
        {
            var Q0;
            Q0=makeQuery(id+"F12.opExtrude","SWEPT_EDGE",EDGE,{"disambiguationData":[OSD([sQuery(id+"F10.wireOp",EDGE,"E14"),sQuery(id+"F10.wireOp",EDGE,"E16.0")])]});
            var Q1;
            Q1=makeQuery(id+"F12.opExtrude","SWEPT_EDGE",EDGE,{"disambiguationData":[OSD([sQuery(id+"F10.wireOp",EDGE,"E13"),sQuery(id+"F10.wireOp",EDGE,"E16.0")])]});
            var Q2;
            Q2=makeQuery(id+"F12.opExtrude","SWEPT_EDGE",EDGE,{"disambiguationData":[OSD([sQuery(id+"F10.wireOp",EDGE,"E13"),sQuery(id+"F10.wireOp",EDGE,"E18.0")])]});
            var Q3;
            Q3=makeQuery(id+"F12.opExtrude","SWEPT_EDGE",EDGE,{"disambiguationData":[OSD([sQuery(id+"F10.wireOp",EDGE,"E14"),sQuery(id+"F10.wireOp",EDGE,"E18.0")])]});
            fillet(context, id + "F13", {"entities" : qUnion([Q0, Q1, Q2, Q3]), "radius" : 5 * mm, "tangentPropagation" : true, "allowEdgeOverflow" : false});
        }
        {
            var Q0;
            Q0=makeQuery(id+"F12.opExtrude","SWEPT_BODY",BODY,{"disambiguationData":[OSD([sQuery(id+"F10.wireOp",EDGE,"E13"),sQuery(id+"F10.wireOp",EDGE,"E14"),sQuery(id+"F10.wireOp",EDGE,"E16.0"),sQuery(id+"F10.wireOp",EDGE,"E18.0")])]});
            var Q1;
            Q1=makeQuery(id+"F11.boolean.opBoolean","INTERSECT",EDGE,{"derivedFrom":[makeQuery(id+"F7.opExtrude","CAP_FACE",FACE,{"disambiguationData":[OSD([sQuery(id+"F3.wireOp",EDGE,"E10")])],"isStart":false}),makeQuery(id+"F11.opExtrude","SWEPT_FACE",FACE,{"disambiguationData":[OSD([sQuery(id+"F10.wireOp",EDGE,"E12")])]})]});
            circularPattern(context, id + "F14", {"entities" : qUnion([Q0]), "axis" : qUnion([Q1]), "angle" : 360 * degree, "instanceCount" : getVariable(context, 'SP'), "equalSpace" : true});
        }
        {
            var Q0;
            Q0=makeQuery(id+"F14.opPattern","COPY",BODY,{"derivedFrom":makeQuery(id+"F12.opExtrude","SWEPT_BODY",BODY,{"disambiguationData":[OSD([sQuery(id+"F10.wireOp",EDGE,"E13"),sQuery(id+"F10.wireOp",EDGE,"E14"),sQuery(id+"F10.wireOp",EDGE,"E16.0"),sQuery(id+"F10.wireOp",EDGE,"E18.0")])]}),"instanceName":"2"});
            var Q1;
            Q1=makeQuery(id+"F14.opPattern","COPY",BODY,{"derivedFrom":makeQuery(id+"F12.opExtrude","SWEPT_BODY",BODY,{"disambiguationData":[OSD([sQuery(id+"F10.wireOp",EDGE,"E13"),sQuery(id+"F10.wireOp",EDGE,"E14"),sQuery(id+"F10.wireOp",EDGE,"E16.0"),sQuery(id+"F10.wireOp",EDGE,"E18.0")])]}),"instanceName":"1"});
            var Q2;
            Q2=makeQuery(id+"F12.opExtrude","SWEPT_BODY",BODY,{"disambiguationData":[OSD([sQuery(id+"F10.wireOp",EDGE,"E13"),sQuery(id+"F10.wireOp",EDGE,"E14"),sQuery(id+"F10.wireOp",EDGE,"E16.0"),sQuery(id+"F10.wireOp",EDGE,"E18.0")])]});
            var Q3;
            Q3=makeQuery(id+"F14.opPattern","COPY",BODY,{"derivedFrom":makeQuery(id+"F12.opExtrude","SWEPT_BODY",BODY,{"disambiguationData":[OSD([sQuery(id+"F10.wireOp",EDGE,"E13"),sQuery(id+"F10.wireOp",EDGE,"E14"),sQuery(id+"F10.wireOp",EDGE,"E16.0"),sQuery(id+"F10.wireOp",EDGE,"E18.0")])]}),"instanceName":"3"});
            var Q4;
            Q4=makeQuery(id+"F14.opPattern","COPY",BODY,{"derivedFrom":makeQuery(id+"F12.opExtrude","SWEPT_BODY",BODY,{"disambiguationData":[OSD([sQuery(id+"F10.wireOp",EDGE,"E13"),sQuery(id+"F10.wireOp",EDGE,"E14"),sQuery(id+"F10.wireOp",EDGE,"E16.0"),sQuery(id+"F10.wireOp",EDGE,"E18.0")])]}),"instanceName":"4"});
            var Q5;
            Q5=makeQuery(id+"F14.opPattern","COPY",BODY,{"derivedFrom":makeQuery(id+"F12.opExtrude","SWEPT_BODY",BODY,{"disambiguationData":[OSD([sQuery(id+"F10.wireOp",EDGE,"E13"),sQuery(id+"F10.wireOp",EDGE,"E14"),sQuery(id+"F10.wireOp",EDGE,"E16.0"),sQuery(id+"F10.wireOp",EDGE,"E18.0")])]}),"instanceName":"5"});
            var Q6;
            Q6=makeQuery(id+"F7.opExtrude","SWEPT_BODY",BODY,{"disambiguationData":[OSD([sQuery(id+"F3.wireOp",EDGE,"E10")])]});
            booleanBodies(context, id + "F15", {"operationType" : BooleanOperationType.SUBTRACTION, "tools" : qUnion([Q0, Q1, Q2, Q3, Q4, Q5]), "targets" : qUnion([Q6])});
        }
    });
